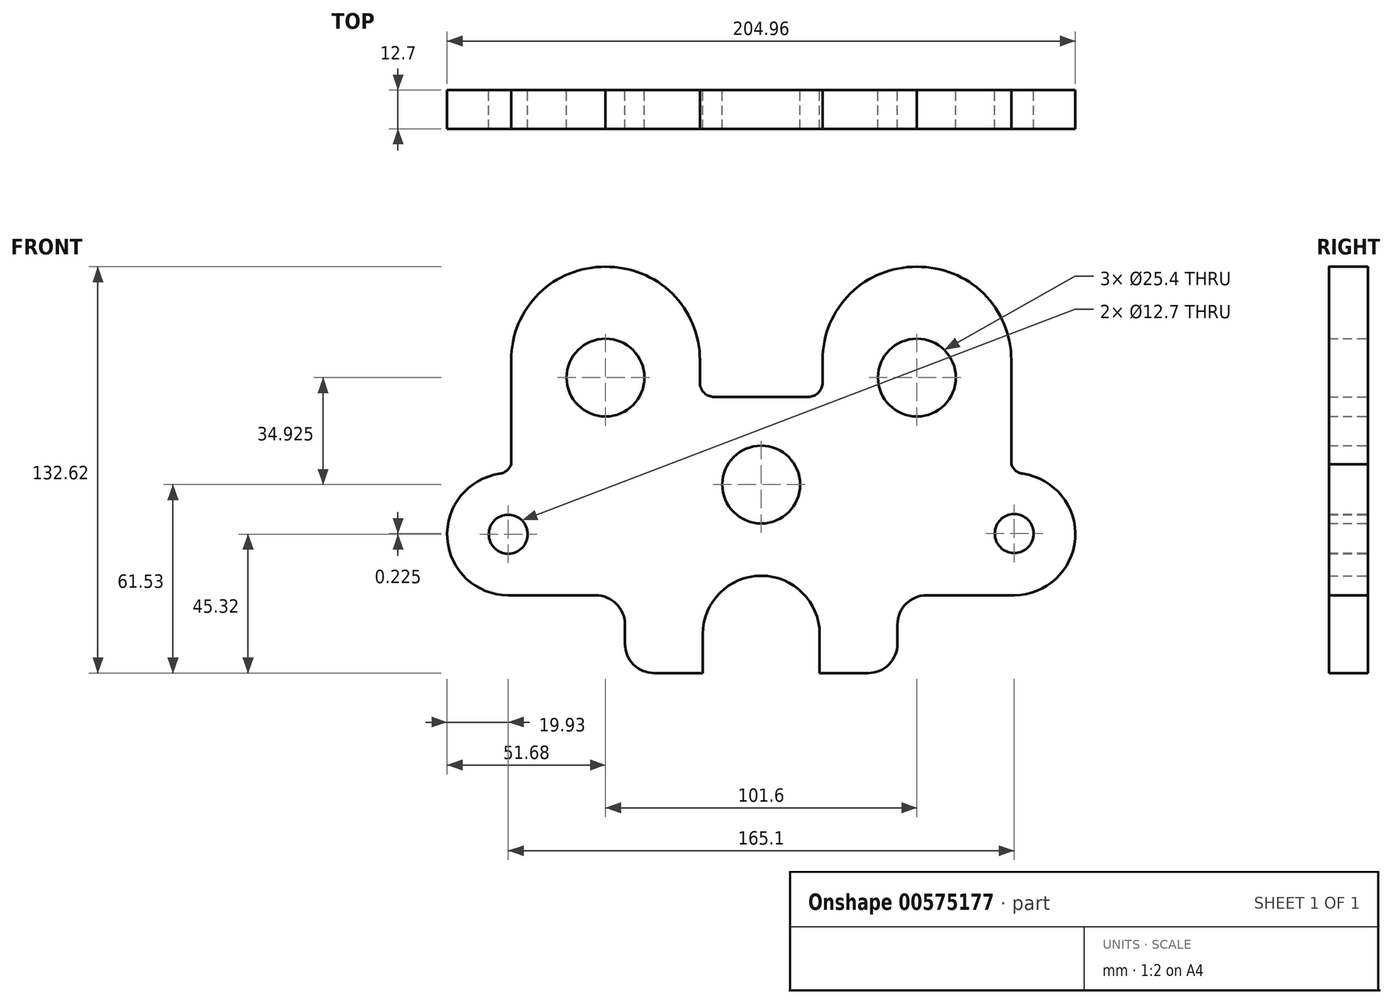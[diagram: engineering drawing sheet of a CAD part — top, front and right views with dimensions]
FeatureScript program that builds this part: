
annotation { "Feature Type Name" : "Feature", "Feature Type Description" : "" }
export const myFeature = defineFeature(function(context is Context, id is Id, definition is map)
    precondition{}
    {
        {
            var Q0;
            Q0=qCreatedBy(makeId("Front.planeOp"),FACE);
            var sketch = newSketch(context, id + "F0", { "sketchPlane" : qUnion([Q0])});
            skCircle(sketch, "E0", {"center": v(0, 0) * mm, "radius": 12.7 * mm});
            skCircle(sketch, "E1", {"center": v(-50.8, 34.92) * mm, "radius": 12.7 * mm});
            skCircle(sketch, "E2", {"center": v(50.8, 34.93) * mm, "radius": 12.7 * mm});
            skCircle(sketch, "E3", {"center": v(-82.55, -16.21) * mm, "radius": 6.35 * mm});
            skCircle(sketch, "E4", {"center": v(82.55, -15.99) * mm, "radius": 6.35 * mm});
            skLineSegment(sketch, "E5", {"start": v(-50.8, 34.92) * mm, "end": v(-50.8, 71.09) * mm, "construction": true});
            skLineSegment(sketch, "E6", {"start": v(50.8, 34.93) * mm, "end": v(104.97, 34.93) * mm, "construction": true});
            skPoint(sketch, "E7", {"position": v(77.89, 34.93) * mm});
            skLineSegment(sketch, "E8", {"start": v(-82.55, -16.21) * mm, "end": v(-82.55, 0) * mm, "construction": true});
            skArc(sketch, "E9", {"start": v(-85.38, 3.52) * mm, "mid": v(-102.43, -17.63) * mm, "end": v(-82.55, -36.14) * mm});
            skLineSegment(sketch, "E10", {"start": v(-82.55, -36.14) * mm, "end": v(-82.55, -36.14) * mm});
            skArc(sketch, "E11.MirrorCS", {"start": v(85.38, 3.52) * mm, "mid": v(102.43, -17.63) * mm, "end": v(82.55, -36.14) * mm});
            skLineSegment(sketch, "E12.MirrorCS", {"start": v(82.55, -36.14) * mm, "end": v(82.55, -36.14) * mm});
            skLineSegment(sketch, "E13", {"start": v(-82.55, -36.14) * mm, "end": v(-53.98, -36.14) * mm});
            skLineSegment(sketch, "E14.MirrorCS", {"start": v(82.55, -36.14) * mm, "end": v(53.98, -36.14) * mm});
            skArc(sketch, "E15", {"start": v(-50.8, 71.09) * mm, "mid": v(-29.05, 62.34) * mm, "end": v(-20, 40.71) * mm});
            skArc(sketch, "E16.MirrorCS", {"start": v(50.8, 71.09) * mm, "mid": v(29.05, 62.34) * mm, "end": v(20, 40.71) * mm});
            skLineSegment(sketch, "E17", {"start": v(-82.55, 3.72) * mm, "end": v(-82.55, 3.72) * mm});
            skLineSegment(sketch, "E18.MirrorCS", {"start": v(82.55, 3.72) * mm, "end": v(82.55, 3.72) * mm});
            skLineSegment(sketch, "E19", {"start": v(-20, 40.71) * mm, "end": v(-20, 33.34) * mm});
            skLineSegment(sketch, "E20.MirrorCS", {"start": v(20, 40.71) * mm, "end": v(20, 33.34) * mm});
            skLineSegment(sketch, "E21", {"start": v(-15.25, 28.58) * mm, "end": v(15.25, 28.58) * mm});
            skLineSegment(sketch, "E22", {"start": v(-34.93, -61.53) * mm, "end": v(-19.05, -61.53) * mm});
            skLineSegment(sketch, "E23", {"start": v(-19.05, -48.83) * mm, "end": v(-19.05, -61.53) * mm});
            skLineSegment(sketch, "E24.MirrorCS", {"start": v(19.05, -48.83) * mm, "end": v(19.05, -61.53) * mm});
            skLineSegment(sketch, "E25.MirrorCS", {"start": v(34.93, -61.53) * mm, "end": v(19.05, -61.53) * mm});
            skArc(sketch, "E26", {"start": v(-19.05, -48.83) * mm, "mid": v(-13.47, -35.36) * mm, "end": v(0, -29.78) * mm});
            skArc(sketch, "E27.MirrorCS", {"start": v(19.05, -48.83) * mm, "mid": v(13.47, -35.36) * mm, "end": v(0, -29.78) * mm});
            skLineSegment(sketch, "E28", {"start": v(-44.45, -44.96) * mm, "end": v(-44.45, -45.67) * mm});
            skLineSegment(sketch, "E29", {"start": v(-44.45, -44.96) * mm, "end": v(-44.45, -52) * mm});
            skLineSegment(sketch, "E30.MirrorCS", {"start": v(44.45, -44.96) * mm, "end": v(44.45, -45.67) * mm});
            skLineSegment(sketch, "E31.MirrorCS", {"start": v(44.45, -44.96) * mm, "end": v(44.45, -52) * mm});
            skPoint(sketch, "E32.visualSharp", {"position": v(-20, 28.57) * mm});
            skArc(sketch, "E32.filletArc", {"start": v(-20, 33.34) * mm, "mid": v(-18.61, 29.97) * mm, "end": v(-15.25, 28.57) * mm});
            skPoint(sketch, "E33.visualSharp", {"position": v(20, 28.57) * mm});
            skArc(sketch, "E33.filletArc", {"start": v(15.25, 28.57) * mm, "mid": v(18.61, 29.97) * mm, "end": v(20, 33.34) * mm});
            skPoint(sketch, "E34.visualSharp", {"position": v(-82.55, 3.72) * mm});
            skArc(sketch, "E34.filletArc", {"start": v(-85.38, 3.52) * mm, "mid": v(-83.07, 4.53) * mm, "end": v(-81.6, 6.58) * mm});
            skPoint(sketch, "E35.visualSharp", {"position": v(82.55, 3.72) * mm});
            skArc(sketch, "E35.filletArc", {"start": v(81.6, 6.57) * mm, "mid": v(83.07, 4.52) * mm, "end": v(85.38, 3.52) * mm});
            skPoint(sketch, "E36.visualSharp", {"position": v(-44.45, -61.53) * mm});
            skArc(sketch, "E36.filletArc", {"start": v(-44.45, -52) * mm, "mid": v(-41.66, -58.74) * mm, "end": v(-34.93, -61.53) * mm});
            skPoint(sketch, "E37.visualSharp", {"position": v(44.45, -61.53) * mm});
            skArc(sketch, "E37.filletArc", {"start": v(34.93, -61.53) * mm, "mid": v(41.66, -58.74) * mm, "end": v(44.45, -52) * mm});
            skPoint(sketch, "E38.visualSharp", {"position": v(-44.45, -36.14) * mm});
            skArc(sketch, "E38.filletArc", {"start": v(-44.45, -45.67) * mm, "mid": v(-47.24, -38.93) * mm, "end": v(-53.98, -36.14) * mm});
            skPoint(sketch, "E39.visualSharp", {"position": v(44.45, -36.14) * mm});
            skArc(sketch, "E39.filletArc", {"start": v(53.98, -36.14) * mm, "mid": v(47.24, -38.93) * mm, "end": v(44.45, -45.67) * mm});
            skArc(sketch, "E40.MirrorCS", {"start": v(-50.8, 71.09) * mm, "mid": v(-72.55, 62.34) * mm, "end": v(-81.6, 40.71) * mm});
            skLineSegment(sketch, "E41", {"start": v(-81.6, 40.71) * mm, "end": v(-81.6, 6.58) * mm});
            skArc(sketch, "E42.MirrorCS", {"start": v(50.8, 71.09) * mm, "mid": v(72.55, 62.34) * mm, "end": v(81.6, 40.71) * mm});
            skLineSegment(sketch, "E43", {"start": v(81.6, 40.71) * mm, "end": v(81.6, 6.57) * mm});
            skCircle(sketch, "E44", {"center": v(82.55, -15.99) * mm, "radius": 7.94 * mm});
            skCircle(sketch, "E45", {"center": v(-82.55, -15.99) * mm, "radius": 7.94 * mm});
            skSolve(sketch);
        }
        {
            var Q0;
            Q0=qSketchRegion(id+"F0",true);
            var Q1;
            Q1=makeQuery(id+"F0.imprint","IMPRINT",FACE,{"disambiguationData":[TD([[makeQuery(id+"F0.imprint","IMPRINT",EDGE,{"derivedFrom":sQuery(id+"F0.wireOp",EDGE,"E3")}),-1.0]])]});
            var Q2;
            Q2=makeQuery(id+"F0.imprint","IMPRINT",FACE,{"disambiguationData":[TD([[makeQuery(id+"F0.imprint","IMPRINT",EDGE,{"derivedFrom":sQuery(id+"F0.wireOp",EDGE,"E4")}),-1.0]])]});
            extrude(context, id + "F1", {"entities" : qUnion([Q0, Q1, Q2]), "depth" : 12.7 * mm, "offsetDistance" : 25.4 * mm});
        }
    });
